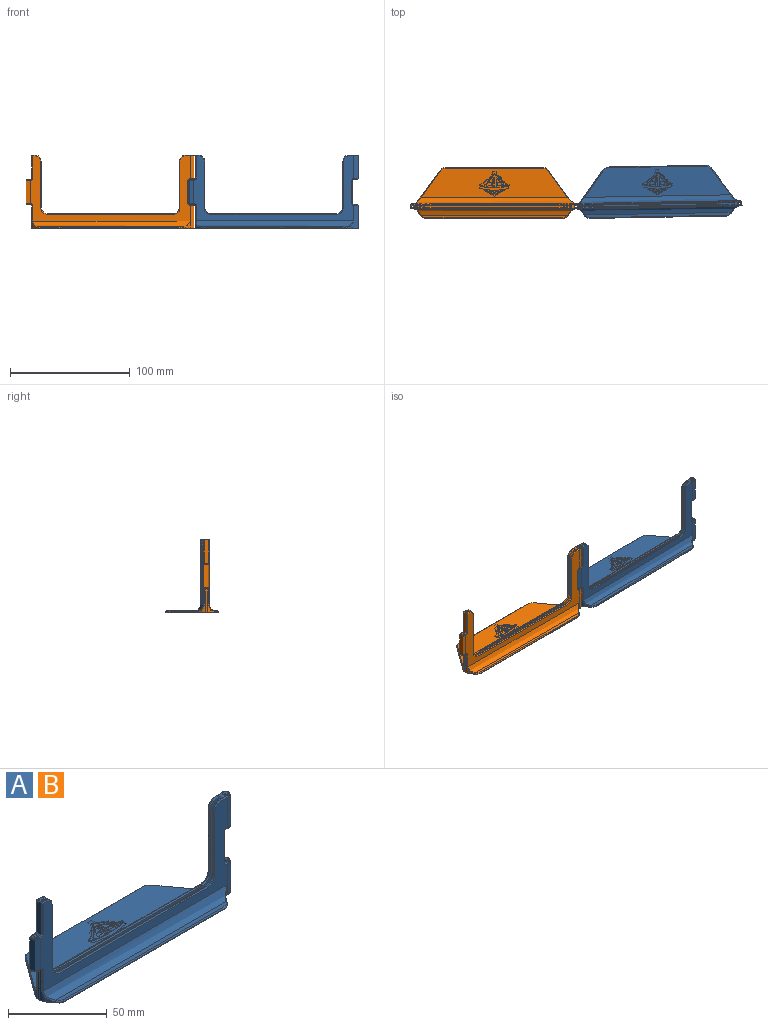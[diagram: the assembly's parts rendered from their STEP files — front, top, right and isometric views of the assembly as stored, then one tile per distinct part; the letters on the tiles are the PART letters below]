
ASSEMBLY  parts=2 mates=1
PART A: 291 faces, bbox 142.1x42.8x61.7 mm
  f0: plane 134.05x54.48mm, normal (0,-1,0), area 1465.1mm2, adj f27,f31,f36,f44,f75,f84,f85,f86
  f1: plane 134.05x54.48mm, normal (0,1,0), area 1465.1mm2, adj f27,f31,f36,f39,f90,f92,f93,f102
  f2: plane 19.38x3.49mm, normal (-1,0,0), area 67.6mm2, adj f120,f121,f127,f128
  f3: plane 59.4x1.35mm, normal (-1,0,0), area 80.2mm2, adj f10,f11,f15,f57
  f4: plane 59.4x1.35mm, normal (1,0,0), area 80.2mm2, adj f10,f11,f15,f72
  f5: plane 3.49x2.22mm, normal (0,0,1), area 3.3mm2, adj f47,f54,f70,f72,f74,f122,f128,f132
  f6: plane 19.38x1.44mm, normal (-1,0,0), area 27.9mm2, adj f37,f42,f89,f158
  f7: plane 135.28x41.49mm, normal (0,0,-1), area 4714.4mm2, adj f147,f148,f149,f150,f151,f152,f153,f154
  f8: plane 19.53x3.49mm, normal (1,0,0), area 68.2mm2, adj f135,f140,f143,f146
  f9: plane 7.76x4.19mm, normal (0,0,1), area 14.5mm2, adj f49,f51,f55,f57,f59,f105,f107,f109
  f10: plane 127.6x1.35mm, normal (0,0,1), area 172.3mm2, adj f3,f4,f11,f15
  f11: plane 127.6x59.4mm, normal (0,1,0), area 1876.1mm2, adj f3,f4,f10,f55,f56,f58,f60,f62
  f12: plane 39x0.47mm, normal (-1,0,0), area 18.3mm2, adj f51,f52,f58,f114
  f13: plane 105.3x0.47mm, normal (0,0,1), area 49.5mm2, adj f52,f53,f62,f123
  f14: plane 39x0.47mm, normal (1,0,0), area 18.3mm2, adj f53,f54,f66,f129
  f15: plane 127.6x59.4mm, normal (0,-1,0), area 1876.1mm2, adj f3,f4,f10,f59,f61,f63,f65,f67
  f16: plane 39x0.47mm, normal (-1,0,0), area 18.3mm2, adj f49,f50,f63,f104
  f17: plane 105.3x0.47mm, normal (0,0,1), area 49.5mm2, adj f48,f50,f67,f108
  f18: plane 39x0.47mm, normal (1,0,0), area 18.3mm2, adj f47,f48,f71,f113
  f19: plane 122.19x24.4mm, normal (0,0,1), area 2364mm2, adj f39,f96,f97,f98,f99,f100,f169,f170
  f20: plane 26.02x18.91mm, normal (0.81,0.59,0), area 14.4mm2, adj f38,f40,f100,f101,f147
  f21: plane 26.65x19.37mm, normal (-0.81,0.59,0), area 15.8mm2, adj f37,f41,f95,f96,f154
  f22: plane 82.25x0.4mm, normal (0,1,0), area 32.9mm2, adj f40,f41,f98,f150
  f23: plane 122.19x2.4mm, normal (0,0,1), area 287.6mm2, adj f44,f77,f78,f79,f80,f81
  f24: plane 4.02x2.92mm, normal (0.81,-0.59,0), area 3.5mm2, adj f43,f45,f76,f77,f155
  f25: plane 114.22x0.4mm, normal (0,-1,0), area 45.7mm2, adj f45,f46,f79,f159
  f26: plane 4.65x3.38mm, normal (-0.81,-0.59,0), area 4.9mm2, adj f42,f46,f81,f82,f162
  f27: cylinder r=2.69mm len=19.23mm, axis (0,0,-1), area 216.3mm2, adj f0,f1,f38,f43,f75,f102,f137,f151
  f28: cylinder r=1.03mm len=19.23mm, axis (0,0,-1), area 123.9mm2, adj f163,f167
  f29: plane 4.34x4.19mm, normal (0,0,1), area 7mm2, adj f133,f137,f140,f141,f167
  f30: plane 4.34x4.19mm, normal (0,0,-1), area 7mm2, adj f134,f138,f142,f143,f166
  f31: cylinder r=2.69mm len=19.23mm, axis (0,0,-1), area 216.3mm2, adj f0,f1,f107,f138
  f32: cylinder r=1.03mm len=19.23mm, axis (0,0,-1), area 123.9mm2, adj f166,f168
  f33: plane 4.34x4.19mm, normal (0,0,1), area 7mm2, adj f112,f115,f119,f120,f165
  f34: plane 4.43x4.19mm, normal (0,0,-1), area 7mm2, adj f86,f87,f88,f89,f90,f91,f164
  f35: cylinder r=1.03mm len=19.23mm, axis (0,0,-1), area 123.9mm2, adj f164,f165
  f36: cylinder r=2.69mm len=19.23mm, axis (0,0,-1), area 216.3mm2, adj f0,f1,f88,f115
  f37: cylinder r=5mm len=19.38mm, axis (0,0,1), area 30.8mm2, adj f6,f21,f91,f93,f94,f156
  f38: cylinder r=5mm len=5.59mm, axis (0,0,-1), area 12.8mm2, adj f20,f27,f102,f149
  f39: cylinder r=5mm len=131.67mm, axis (1,0,0), area 1001.3mm2, adj f1,f19,f94,f95,f101,f102
  f40: cylinder r=5mm len=4.05mm, axis (0,0,1), area 1.9mm2, adj f20,f22,f99,f148
  f41: cylinder r=5mm len=4.05mm, axis (0,0,-1), area 1.9mm2, adj f21,f22,f97,f152
  f42: cylinder r=5mm len=19.38mm, axis (0,0,-1), area 30.8mm2, adj f6,f26,f83,f84,f87,f160
  f43: cylinder r=5mm len=5.59mm, axis (0,0,-1), area 12.8mm2, adj f24,f27,f75,f153
  f44: cylinder r=5mm len=131.67mm, axis (1,0,0), area 1001.3mm2, adj f0,f23,f75,f76,f82,f83
  f45: cylinder r=5mm len=4.05mm, axis (0,0,-1), area 1.9mm2, adj f24,f25,f78,f157
  f46: cylinder r=5mm len=4.05mm, axis (0,0,1), area 1.9mm2, adj f25,f26,f80,f161
  f47: cylinder r=5mm len=5mm, axis (0,-1,0), area 3.7mm2, adj f5,f18,f73,f117
  f48: cylinder r=5mm len=5mm, axis (0,-1,0), area 3.7mm2, adj f17,f18,f69,f110
  f49: cylinder r=5mm len=5mm, axis (0,-1,0), area 3.7mm2, adj f9,f16,f61,f103
  f50: cylinder r=5mm len=5mm, axis (0,1,0), area 3.7mm2, adj f16,f17,f65,f106
  f51: cylinder r=5mm len=5mm, axis (0,1,0), area 3.7mm2, adj f9,f12,f56,f111
  f52: cylinder r=5mm len=5mm, axis (0,-1,0), area 3.7mm2, adj f12,f13,f60,f118
  f53: cylinder r=5mm len=5mm, axis (0,1,0), area 3.7mm2, adj f13,f14,f64,f126
  f54: cylinder r=5mm len=5mm, axis (0,1,0), area 3.7mm2, adj f5,f14,f68,f131
  f55: plane 1.75x0.6mm, normal (0,0.71,0.71), area 1.2mm2, adj f9,f11,f56,f57
  f56: cone r=4.4mm half-angle=45deg, axis (0,-1,0), area 6.3mm2, adj f11,f51,f55,f58
  f57: plane 2.55x0.6mm, normal (-0.71,0,0.71), area 1.7mm2, adj f3,f9,f55,f59
  f58: plane 39x0.6mm, normal (-0.71,0.71,0), area 33.1mm2, adj f11,f12,f56,f60
  f59: plane 1.75x0.6mm, normal (0,-0.71,0.71), area 1.2mm2, adj f9,f15,f57,f61
  f60: cone r=5.6mm half-angle=45deg, axis (0,1,0), area 7.1mm2, adj f11,f52,f58,f62
  f61: cone r=4.4mm half-angle=45deg, axis (0,1,0), area 6.3mm2, adj f15,f49,f59,f63
  f62: plane 105.3x0.6mm, normal (0,0.71,0.71), area 89.4mm2, adj f11,f13,f60,f64
  f63: plane 39x0.6mm, normal (-0.71,-0.71,0), area 33.1mm2, adj f15,f16,f61,f65
  f64: cone r=5.6mm half-angle=45deg, axis (0,1,0), area 7.1mm2, adj f11,f53,f62,f66
  f65: cone r=5.6mm half-angle=45deg, axis (0,-1,0), area 7.1mm2, adj f15,f50,f63,f67
  f66: plane 39x0.6mm, normal (0.71,0.71,0), area 33.1mm2, adj f11,f14,f64,f68
  f67: plane 105.3x0.6mm, normal (0,-0.71,0.71), area 89.4mm2, adj f15,f17,f65,f69
  f68: cone r=4.4mm half-angle=45deg, axis (0,-1,0), area 6.3mm2, adj f11,f54,f66,f70
  f69: cone r=5.6mm half-angle=45deg, axis (0,-1,0), area 7.1mm2, adj f15,f48,f67,f71
  f70: plane 1.75x0.6mm, normal (0,0.71,0.71), area 1.2mm2, adj f5,f11,f68,f72
  f71: plane 39x0.6mm, normal (0.71,-0.71,0), area 33.1mm2, adj f15,f18,f69,f73
  f72: plane 2.55x0.6mm, normal (0.71,0,0.71), area 1.7mm2, adj f4,f5,f70,f74
  f73: cone r=4.4mm half-angle=45deg, axis (0,1,0), area 6.3mm2, adj f15,f47,f71,f74
  f74: plane 1.75x0.6mm, normal (0,-0.71,0.71), area 1.2mm2, adj f5,f15,f72,f73
  f75: bspline ~4.88x3.58mm, area 2.3mm2, adj f0,f27,f43,f44,f76
  f76: bspline ~3.42x2.97mm, area 3.3mm2, adj f24,f44,f75,f77
  f77: plane 0.94x0.91mm, normal (0.57,-0.42,0.71), area 0.6mm2, adj f23,f24,f76,f78
  f78: cone r=4.4mm half-angle=45deg, axis (0,0,-1), area 3.8mm2, adj f23,f45,f77,f79
  f79: plane 114.22x0.6mm, normal (0,-0.71,0.71), area 96.9mm2, adj f23,f25,f78,f80
  f80: cone r=4.4mm half-angle=45deg, axis (0,0,-1), area 3.8mm2, adj f23,f46,f79,f81
  f81: plane 0.94x0.91mm, normal (-0.57,-0.42,0.71), area 0.6mm2, adj f23,f26,f80,f82
  f82: bspline ~4.04x3.42mm, area 3.9mm2, adj f26,f44,f81,f83
  f83: bspline ~3.88x1.88mm, area 3mm2, adj f42,f44,f82,f84
  f84: plane 13.38x0.58mm, normal (-0.62,-0.79,0), area 9.9mm2, adj f0,f42,f83,f85
  f85: bspline ~1.23x1.2mm, area 0.9mm2, adj f0,f84,f86,f87
  f86: plane 1.2x0.62mm, normal (0,-0.71,-0.71), area 0.9mm2, adj f0,f34,f85,f88
  f87: cone r=5.6mm half-angle=45deg, axis (0,0,1), area 0.9mm2, adj f34,f42,f85,f89
  f88: cone r=2.1mm half-angle=45deg, axis (0,0,1), area 8.6mm2, adj f34,f36,f86,f90
  f89: plane 1.44x0.6mm, normal (-0.71,0,-0.71), area 1.2mm2, adj f6,f34,f87,f91
  f90: plane 1.2x0.62mm, normal (0,0.71,-0.71), area 0.9mm2, adj f1,f34,f88,f92
  f91: cone r=5.6mm half-angle=45deg, axis (0,0,1), area 0.9mm2, adj f34,f37,f89,f92
  f92: bspline ~1.23x1.2mm, area 0.9mm2, adj f1,f90,f91,f93
  f93: plane 13.38x0.58mm, normal (-0.62,0.79,0), area 9.9mm2, adj f1,f37,f92,f94
  f94: bspline ~3.88x1.87mm, area 3mm2, adj f37,f39,f93,f95
  f95: bspline ~4.04x3.42mm, area 3.9mm2, adj f21,f39,f94,f96
  f96: plane 22.94x16.9mm, normal (-0.57,0.42,0.71), area 23.7mm2, adj f19,f21,f95,f97
  f97: cone r=4.4mm half-angle=45deg, axis (0,0,-1), area 3.8mm2, adj f19,f41,f96,f98
  f98: plane 82.25x0.6mm, normal (0,0.71,0.71), area 69.8mm2, adj f19,f22,f97,f99
  f99: cone r=4.4mm half-angle=45deg, axis (0,0,-1), area 3.8mm2, adj f19,f40,f98,f100
  f100: plane 22.94x16.9mm, normal (0.57,0.42,0.71), area 23.7mm2, adj f19,f20,f99,f101
  f101: bspline ~3.42x2.97mm, area 3.3mm2, adj f20,f39,f100,f102
  f102: bspline ~4.88x3.58mm, area 2.3mm2, adj f1,f27,f38,f39,f101
  f103: cone r=4.4mm half-angle=45deg, axis (0,-1,0), area 6.3mm2, adj f1,f49,f104,f105
  f104: plane 39x0.6mm, normal (-0.71,0.71,0), area 33.1mm2, adj f1,f16,f103,f106
  f105: plane 4.52x0.62mm, normal (0,0.71,0.71), area 3.7mm2, adj f1,f9,f103,f107
  f106: cone r=5.6mm half-angle=45deg, axis (0,1,0), area 7.1mm2, adj f1,f50,f104,f108
  f107: cone r=2.1mm half-angle=45deg, axis (0,0,-1), area 8.6mm2, adj f9,f31,f105,f109
  f108: plane 105.3x0.6mm, normal (0,0.71,0.71), area 89.4mm2, adj f1,f17,f106,f110
  f109: plane 4.52x0.62mm, normal (0,-0.71,0.71), area 3.7mm2, adj f0,f9,f107,f111
  f110: cone r=5.6mm half-angle=45deg, axis (0,1,0), area 7.1mm2, adj f1,f48,f108,f113
  f111: cone r=4.4mm half-angle=45deg, axis (0,1,0), area 6.3mm2, adj f0,f51,f109,f114
  f112: plane 1.1x0.62mm, normal (0,0.71,0.71), area 0.8mm2, adj f1,f33,f115,f116
  f113: plane 39x0.6mm, normal (0.71,0.71,0), area 33.1mm2, adj f1,f18,f110,f117
  f114: plane 39x0.6mm, normal (-0.71,-0.71,0), area 33.1mm2, adj f0,f12,f111,f118
  f115: cone r=2.69mm half-angle=45deg, axis (0,0,-1), area 8.6mm2, adj f33,f36,f112,f119
  f116: plane 1.2x1.2mm, normal (-0.58,0.58,0.58), area 0.9mm2, adj f1,f112,f120,f121
  f117: cone r=4.4mm half-angle=45deg, axis (0,-1,0), area 6.3mm2, adj f1,f47,f113,f122
  f118: cone r=5.6mm half-angle=45deg, axis (0,-1,0), area 7.1mm2, adj f0,f52,f114,f123
  f119: plane 1.1x0.62mm, normal (0,-0.71,0.71), area 0.8mm2, adj f0,f33,f115,f124
  f120: plane 3.49x0.6mm, normal (-0.71,0,0.71), area 3mm2, adj f2,f33,f116,f124
  f121: plane 19.38x0.6mm, normal (-0.71,0.71,0), area 16.4mm2, adj f1,f2,f116,f125
  f122: plane 2.22x0.6mm, normal (0,0.71,0.71), area 1.9mm2, adj f1,f5,f117,f125
  f123: plane 105.3x0.6mm, normal (0,-0.71,0.71), area 89.4mm2, adj f0,f13,f118,f126
  f124: plane 1.2x1.2mm, normal (-0.58,-0.58,0.58), area 0.9mm2, adj f0,f119,f120,f127
  f125: plane 0.6x0.6mm, normal (-0.58,0.58,0.58), area 0.3mm2, adj f121,f122,f128
  f126: cone r=5.6mm half-angle=45deg, axis (0,-1,0), area 7.1mm2, adj f0,f53,f123,f129
  f127: plane 19.38x0.6mm, normal (-0.71,-0.71,0), area 16.4mm2, adj f0,f2,f124,f130
  f128: plane 3.49x0.6mm, normal (-0.71,0,0.71), area 3mm2, adj f2,f5,f125,f130
  f129: plane 39x0.6mm, normal (0.71,-0.71,0), area 33.1mm2, adj f0,f14,f126,f131
  f130: plane 0.6x0.6mm, normal (-0.58,-0.58,0.58), area 0.3mm2, adj f127,f128,f132
  f131: cone r=4.4mm half-angle=45deg, axis (0,1,0), area 6.3mm2, adj f0,f54,f129,f132
  f132: plane 2.22x0.6mm, normal (0,-0.71,0.71), area 1.9mm2, adj f0,f5,f130,f131
  f133: plane 1.1x0.62mm, normal (0,0.71,0.71), area 0.8mm2, adj f1,f29,f136,f137
  f134: plane 1.1x0.62mm, normal (0,0.71,-0.71), area 0.8mm2, adj f1,f30,f138,f139
  f135: plane 19.53x0.6mm, normal (0.71,0.71,0), area 16.6mm2, adj f1,f8,f136,f139
  f136: plane 1.2x1.2mm, normal (0.58,0.58,0.58), area 0.9mm2, adj f1,f133,f135,f140
  f137: cone r=2.69mm half-angle=45deg, axis (0,0,-1), area 8.6mm2, adj f27,f29,f133,f141
  f138: cone r=2.69mm half-angle=45deg, axis (0,0,1), area 8.6mm2, adj f30,f31,f134,f142
  f139: plane 1.2x1.2mm, normal (0.58,0.58,-0.58), area 0.9mm2, adj f1,f134,f135,f143
  f140: plane 3.49x0.6mm, normal (0.71,0,0.71), area 3mm2, adj f8,f29,f136,f144
  f141: plane 1.1x0.62mm, normal (0,-0.71,0.71), area 0.8mm2, adj f0,f29,f137,f144
  f142: plane 1.1x0.62mm, normal (0,-0.71,-0.71), area 0.8mm2, adj f0,f30,f138,f145
  f143: plane 3.49x0.6mm, normal (0.71,0,-0.71), area 3mm2, adj f8,f30,f139,f145
  f144: plane 1.2x1.2mm, normal (0.58,-0.58,0.58), area 0.9mm2, adj f0,f140,f141,f146
  f145: plane 1.2x1.2mm, normal (0.58,-0.58,-0.58), area 0.9mm2, adj f0,f142,f143,f146
  f146: plane 19.53x0.6mm, normal (0.71,-0.71,0), area 16.6mm2, adj f0,f8,f144,f145
  f147: plane 26.36x19.38mm, normal (0.57,0.42,-0.71), area 27.3mm2, adj f7,f20,f148,f149
  f148: cone r=4.4mm half-angle=45deg, axis (0,0,1), area 3.8mm2, adj f7,f40,f147,f150
  f149: cone r=5.6mm half-angle=45deg, axis (0,0,-1), area 3.3mm2, adj f7,f38,f147,f151
  f150: plane 82.25x0.6mm, normal (0,0.71,-0.71), area 69.8mm2, adj f7,f22,f148,f152
  f151: cone r=2.1mm half-angle=45deg, axis (0,0,1), area 8.7mm2, adj f7,f27,f149,f153
  f152: cone r=4.4mm half-angle=45deg, axis (0,0,1), area 3.8mm2, adj f7,f41,f150,f154
  f153: cone r=5.6mm half-angle=45deg, axis (0,0,-1), area 3.3mm2, adj f7,f43,f151,f155
  f154: plane 26.98x19.83mm, normal (-0.57,0.42,-0.71), area 27.9mm2, adj f7,f21,f152,f156
  f155: plane 4.36x3.4mm, normal (0.57,-0.42,-0.71), area 4.2mm2, adj f7,f24,f153,f157
  f156: cone r=4.4mm half-angle=45deg, axis (0,0,1), area 2.5mm2, adj f7,f37,f154,f158
  f157: cone r=4.4mm half-angle=45deg, axis (0,0,1), area 3.8mm2, adj f7,f45,f155,f159
  f158: plane 1.44x0.6mm, normal (-0.71,0,-0.71), area 1.2mm2, adj f6,f7,f156,f160
  f159: plane 114.22x0.6mm, normal (0,-0.71,-0.71), area 96.9mm2, adj f7,f25,f157,f161
  f160: cone r=4.4mm half-angle=45deg, axis (0,0,1), area 2.5mm2, adj f7,f42,f158,f162
  f161: cone r=4.4mm half-angle=45deg, axis (0,0,1), area 3.8mm2, adj f7,f46,f159,f162
  f162: plane 4.98x3.85mm, normal (-0.57,-0.42,-0.71), area 4.9mm2, adj f7,f26,f160,f161
  f163: cone r=1.03mm half-angle=45deg, axis (0,0,-1), area 7.1mm2, adj f7,f28
  f164: cone r=1.03mm half-angle=45deg, axis (0,0,-1), area 7.1mm2, adj f34,f35
  f165: cone r=1.62mm half-angle=45deg, axis (0,0,1), area 7.1mm2, adj f33,f35
  f166: cone r=1.62mm half-angle=45deg, axis (0,0,-1), area 7.1mm2, adj f30,f32
  f167: cone r=1.62mm half-angle=45deg, axis (0,0,1), area 7.1mm2, adj f28,f29
  f168: cone r=1.03mm half-angle=45deg, axis (0,0,1), area 7.1mm2, adj f9,f32
  f169: extruded ~0.76x0.6mm, area 0.5mm2, adj f19,f170,f247,f248
  f170: extruded ~3.62x0.6mm, area 2.2mm2, adj f19,f169,f171,f248
  f171: plane 2.59x0.6mm, normal (-1,0.03,0), area 1.6mm2, adj f19,f170,f172,f248
  f172: extruded ~3.53x0.6mm, area 2.1mm2, adj f19,f171,f173,f248
  f173: extruded ~4.22x4.14mm, area 3.7mm2, adj f19,f172,f174,f248
  f174: extruded ~1.1x0.6mm, area 0.7mm2, adj f19,f173,f175,f248
  f175: extruded ~6.71x0.6mm, area 4mm2, adj f19,f174,f176,f248
  f176: plane 1.54x0.6mm, normal (0,1,0), area 0.9mm2, adj f19,f175,f177,f248
  f177: plane 7.42x0.6mm, normal (-1,0.01,0), area 4.5mm2, adj f19,f176,f178,f248
  f178: plane 0.6x0.49mm, normal (0,1,0), area 0.3mm2, adj f19,f177,f179,f248
  f179: plane 7.42x0.6mm, normal (1,0.01,0), area 4.5mm2, adj f19,f178,f180,f248
  f180: plane 1.56x0.6mm, normal (0,1,0), area 0.9mm2, adj f19,f179,f181,f248
  f181: extruded ~6.71x0.6mm, area 4mm2, adj f19,f180,f182,f248
  f182: extruded ~1.07x0.6mm, area 0.6mm2, adj f19,f181,f183,f248
  f183: extruded ~4.13x4.11mm, area 3.6mm2, adj f19,f182,f184,f248
  f184: extruded ~3.44x0.6mm, area 2.1mm2, adj f19,f183,f185,f248
  f185: plane 2.59x0.6mm, normal (1,0.03,0), area 1.6mm2, adj f19,f184,f186,f248
  f186: extruded ~3.54x0.6mm, area 2.1mm2, adj f19,f185,f187,f248
  f187: extruded ~0.78x0.6mm, area 0.5mm2, adj f19,f186,f188,f248
  f188: extruded ~0.6x0.29mm, area 0.2mm2, adj f19,f187,f189,f248
  f189: extruded ~1.68x0.6mm, area 1mm2, adj f19,f188,f190,f248
  f190: extruded ~5.06x2.53mm, area 3.5mm2, adj f19,f189,f191,f248
  f191: plane 0.76x0.6mm, normal (-0.82,0.58,0), area 0.6mm2, adj f19,f190,f192,f248
  f192: extruded ~5.89x2.98mm, area 4.1mm2, adj f19,f191,f193,f248
  f193: extruded ~1.48x0.6mm, area 0.9mm2, adj f19,f192,f194,f248
  f194: extruded ~0.62x0.6mm, area 0.4mm2, adj f19,f193,f195,f248
  f195: extruded ~1.4x0.6mm, area 0.8mm2, adj f19,f194,f196,f248
  f196: extruded ~6.38x3.23mm, area 4.4mm2, adj f19,f195,f197,f248
  f197: plane 0.6x0.45mm, normal (-0.82,0.58,0), area 0.3mm2, adj f19,f196,f198,f248
  f198: extruded ~6.83x3.46mm, area 4.8mm2, adj f19,f197,f199,f248
  f199: extruded ~1.31x0.6mm, area 0.8mm2, adj f19,f198,f200,f248
  f200: extruded ~0.6x0.02mm, area 0mm2, adj f19,f199,f201,f248
  f201: extruded ~0.9x0.6mm, area 0.5mm2, adj f19,f200,f202,f248
  f202: plane 0.6x0mm, normal (-0.99,0.12,0), area 0mm2, adj f201,f203
  f203: extruded ~3.2x1.1mm, area 2mm2, adj f19,f202,f204,f248
  f204: extruded ~0.6x0.12mm, area 0.1mm2, adj f19,f203,f205,f248
  f205: extruded ~0.6x0.06mm, area 0mm2, adj f19,f204,f206,f248
  f206: extruded ~3.18x1.18mm, area 2.1mm2, adj f19,f205,f207,f248
  f207: extruded ~9.26x8.04mm, area 8mm2, adj f19,f206,f208,f248
  f208: extruded ~9.26x8.06mm, area 8mm2, adj f19,f207,f209,f248
  f209: extruded ~3.17x1.19mm, area 2.1mm2, adj f19,f208,f210,f248
  f210: extruded ~0.6x0.11mm, area 0.1mm2, adj f19,f209,f211,f248
  f211: extruded ~3.56x1.19mm, area 2.3mm2, adj f19,f210,f212,f248
  f212: extruded ~0.6x0mm, area 0mm2, adj f19,f211,f213,f248
  f213: extruded ~0.6x0.47mm, area 0.3mm2, adj f19,f212,f214,f248
  f214: extruded ~1.3x0.6mm, area 0.8mm2, adj f19,f213,f215,f248
  f215: extruded ~8.46x8.46mm, area 8mm2, adj f19,f214,f216,f248
  f216: extruded ~4.75x1.46mm, area 3mm2, adj f19,f215,f217,f248
  f217: plane 1.69x1.19mm, normal (0.82,-0.58,0), area 1.2mm2, adj f19,f216,f218,f248
  f218: extruded ~3.01x1.07mm, area 1.9mm2, adj f19,f217,f219,f248
  f219: extruded ~0.6x0.02mm, area 0mm2, adj f19,f218,f220,f248
  f220: extruded ~0.6x0.09mm, area 0.1mm2, adj f19,f219,f221,f248
  f221: extruded ~0.6x0.08mm, area 0mm2, adj f19,f220,f222,f248
  f222: extruded ~0.6x0.07mm, area 0mm2, adj f19,f221,f223,f248
  f223: extruded ~0.6x0.11mm, area 0.1mm2, adj f19,f222,f224,f248
  f224: extruded ~0.6x0.04mm, area 0mm2, adj f19,f223,f225,f248
  f225: extruded ~0.6x0.14mm, area 0.1mm2, adj f19,f224,f226,f248
  f226: extruded ~0.6x0.15mm, area 0.1mm2, adj f19,f225,f227,f248
  f227: extruded ~0.6x0.03mm, area 0mm2, adj f19,f226,f228,f248
  f228: extruded ~0.6x0.14mm, area 0.1mm2, adj f19,f227,f229,f248
  f229: extruded ~0.6x0.03mm, area 0mm2, adj f19,f228,f230,f248
  f230: extruded ~0.6x0.12mm, area 0.1mm2, adj f19,f229,f231,f248
  f231: extruded ~0.6x0.03mm, area 0mm2, adj f19,f230,f232,f248
  f232: extruded ~0.6x0.13mm, area 0.1mm2, adj f19,f231,f233,f248
  f233: extruded ~0.6x0.04mm, area 0mm2, adj f19,f232,f234,f248
  f234: extruded ~0.6x0.11mm, area 0.1mm2, adj f19,f233,f235,f248
  f235: extruded ~0.6x0.04mm, area 0mm2, adj f19,f234,f236,f248
  f236: extruded ~0.6x0.11mm, area 0.1mm2, adj f19,f235,f237,f248
  f237: extruded ~0.6x0.05mm, area 0mm2, adj f19,f236,f238,f248
  f238: extruded ~0.6x0.12mm, area 0.1mm2, adj f19,f237,f239,f248
  f239: extruded ~0.6x0.05mm, area 0mm2, adj f19,f238,f240,f248
  f240: extruded ~0.6x0.08mm, area 0mm2, adj f19,f239,f241,f248
  f241: extruded ~0.6x0.06mm, area 0mm2, adj f19,f240,f242,f248
  f242: extruded ~0.6x0.11mm, area 0.1mm2, adj f19,f241,f243,f248
  f243: extruded ~0.6x0.06mm, area 0mm2, adj f19,f242,f244,f248
  f244: extruded ~0.6x0.07mm, area 0mm2, adj f19,f243,f245,f248
  f245: extruded ~6.14x4.8mm, area 5mm2, adj f19,f244,f246,f248
  f246: extruded ~1.67x0.6mm, area 1mm2, adj f19,f245,f247,f248
  f247: extruded ~0.6x0.29mm, area 0.2mm2, adj f19,f169,f246,f248
  f248: plane 24.94x11.25mm, normal (0,0,1), area 91.1mm2, adj f169,f170,f171,f172,f173,f174,f175,f176
  f249: extruded ~5.55x3.16mm, area 3.9mm2, adj f19,f250,f265,f266
  f250: extruded ~0.83x0.6mm, area 0.5mm2, adj f19,f249,f251,f266
  f251: extruded ~4.89x2.49mm, area 3.4mm2, adj f19,f250,f252,f266
  f252: plane 0.6x0.43mm, normal (-0.96,-0.27,0), area 0.3mm2, adj f19,f251,f253,f266
  f253: plane 1.07x0.6mm, normal (0,-1,0), area 0.6mm2, adj f19,f252,f254,f266
  f254: plane 0.6x0.43mm, normal (0.97,-0.26,0), area 0.3mm2, adj f19,f253,f255,f266
  f255: extruded ~4.87x2.5mm, area 3.4mm2, adj f19,f254,f256,f266
  f256: extruded ~0.83x0.6mm, area 0.5mm2, adj f19,f255,f257,f266
  f257: extruded ~5.54x3.17mm, area 3.9mm2, adj f19,f256,f258,f266
  f258: plane 0.6x0.54mm, normal (0.97,-0.26,0), area 0.3mm2, adj f19,f257,f259,f266
  f259: extruded ~6.13x3.79mm, area 4.5mm2, adj f19,f258,f260,f266
  f260: extruded ~1.14x0.6mm, area 0.7mm2, adj f19,f259,f261,f266
  f261: extruded ~8.23x4.91mm, area 6mm2, adj f19,f260,f262,f266
  f262: extruded ~8.22x4.89mm, area 6mm2, adj f19,f261,f263,f266
  f263: extruded ~1.14x0.6mm, area 0.7mm2, adj f19,f262,f264,f266
  f264: extruded ~6.13x3.78mm, area 4.5mm2, adj f19,f263,f265,f266
  f265: plane 0.6x0.53mm, normal (-0.96,-0.27,0), area 0.3mm2, adj f19,f249,f264,f266
  f266: plane 16.44x4.91mm, normal (0,0,1), area 26mm2, adj f249,f250,f251,f252,f253,f254,f255,f256
  f267: extruded ~0.6x0.5mm, area 0.3mm2, adj f19,f268,f272,f273
  f268: extruded ~3.39x1.04mm, area 2.2mm2, adj f19,f267,f269,f273
  f269: extruded ~3.4x1.04mm, area 2.2mm2, adj f19,f268,f270,f273
  f270: extruded ~0.6x0.5mm, area 0.3mm2, adj f19,f269,f271,f273
  f271: extruded ~3.9x1.34mm, area 2.5mm2, adj f19,f270,f272,f273
  f272: extruded ~3.89x1.34mm, area 2.5mm2, adj f19,f267,f271,f273
  f273: plane 7.79x1.34mm, normal (0,0,1), area 2.1mm2, adj f267,f268,f269,f270,f271,f272
  f274: extruded ~0.6x0.1mm, area 0.1mm2, adj f19,f275,f283,f284
  f275: extruded ~2.45x0.6mm, area 1.5mm2, adj f19,f274,f276,f284
  f276: extruded ~0.6x0.08mm, area 0.1mm2, adj f19,f275,f277,f284
  f277: extruded ~11.9x1.72mm, area 7.3mm2, adj f19,f276,f278,f284
  f278: extruded ~11.9x1.72mm, area 7.3mm2, adj f19,f277,f279,f284
  f279: extruded ~0.6x0.08mm, area 0.1mm2, adj f19,f278,f280,f284
  f280: extruded ~2.45x0.6mm, area 1.5mm2, adj f19,f279,f281,f284
  f281: extruded ~0.6x0.09mm, area 0.1mm2, adj f19,f280,f282,f284
  f282: extruded ~12.28x1.85mm, area 7.5mm2, adj f19,f281,f283,f284
  f283: extruded ~12.27x1.84mm, area 7.5mm2, adj f19,f274,f282,f284
  f284: plane 24.75x4.33mm, normal (0,0,1), area 58.6mm2, adj f274,f275,f276,f277,f278,f279,f280,f281
  f285: extruded ~1.58x0.6mm, area 0.9mm2, adj f19,f286,f289,f290
  f286: extruded ~1.96x0.6mm, area 1.2mm2, adj f19,f285,f287,f290
  f287: plane 2.95x0.6mm, normal (0,-1,0), area 1.8mm2, adj f19,f286,f288,f290
  f288: extruded ~1.95x0.6mm, area 1.2mm2, adj f19,f287,f289,f290
  f289: extruded ~1.49x0.6mm, area 0.9mm2, adj f19,f285,f288,f290
  f290: plane 3.07x1.96mm, normal (0,0,1), area 5.6mm2, adj f285,f286,f287,f288,f289
PART B: same geometry as A
PLACE A rot(axis=(0,0,1),1deg) t=(72.06,-17.3,-4.14)mm
PLACE B t=(-64.56,-18.5,-4.2)mm
MATE revolute A.f164 <-> B.f32  axis (0,0,-1) through (3.75,-18.5,34.68)mm
